# Revit family: BAS-IP_Видеодомофон_AZ-07LL
name_source: partatom
category: Устройства связи
units: mm (PartAtom-declared; Revit-internal decimal feet)

## family parameters
Всегда вертикально = Да
На основе рабочей плоскости = Нет
Общий = Нет
При загрузке вырезать с полостями = Нет
Размер круглого соединителя = Использовать диаметр
Сохранять ориентацию аннотаций = Нет
Тип детали = Нормальный
Точка расчета площади = Нет

## types (2) — shared parameters
ADSK_Единица измерения = шт.
ADSK_Завод-изготовитель = BAS-IP
ADSK_Количество = 1
ADSK_Наименование = IP видеодомофон
Варианты монтажа = Горизонтальный и вертикальный
Встроенная камера = Нет
Габаритные размеры = 195 x 127 x 27 мм
Дисплей = 7" TFT LCD, сенсорный емкостный
Изготовитель = BAS-IP
Питание = PoE, +12 В
Потребление питания = 6 Вт, в режиме ожидания - 2,5 Вт
Разрешение экрана = 800 x 480
Тип установки = Настенный накладной
Цветовое решение = Белый

## per-type parameters (varying)
| type | ADSK_Марка | ADSK_Материал | Корпус |
| Белый | AZ-07LL White | White | Пластик |
| Черный | AZ-07LL Black | Black | Черный |
